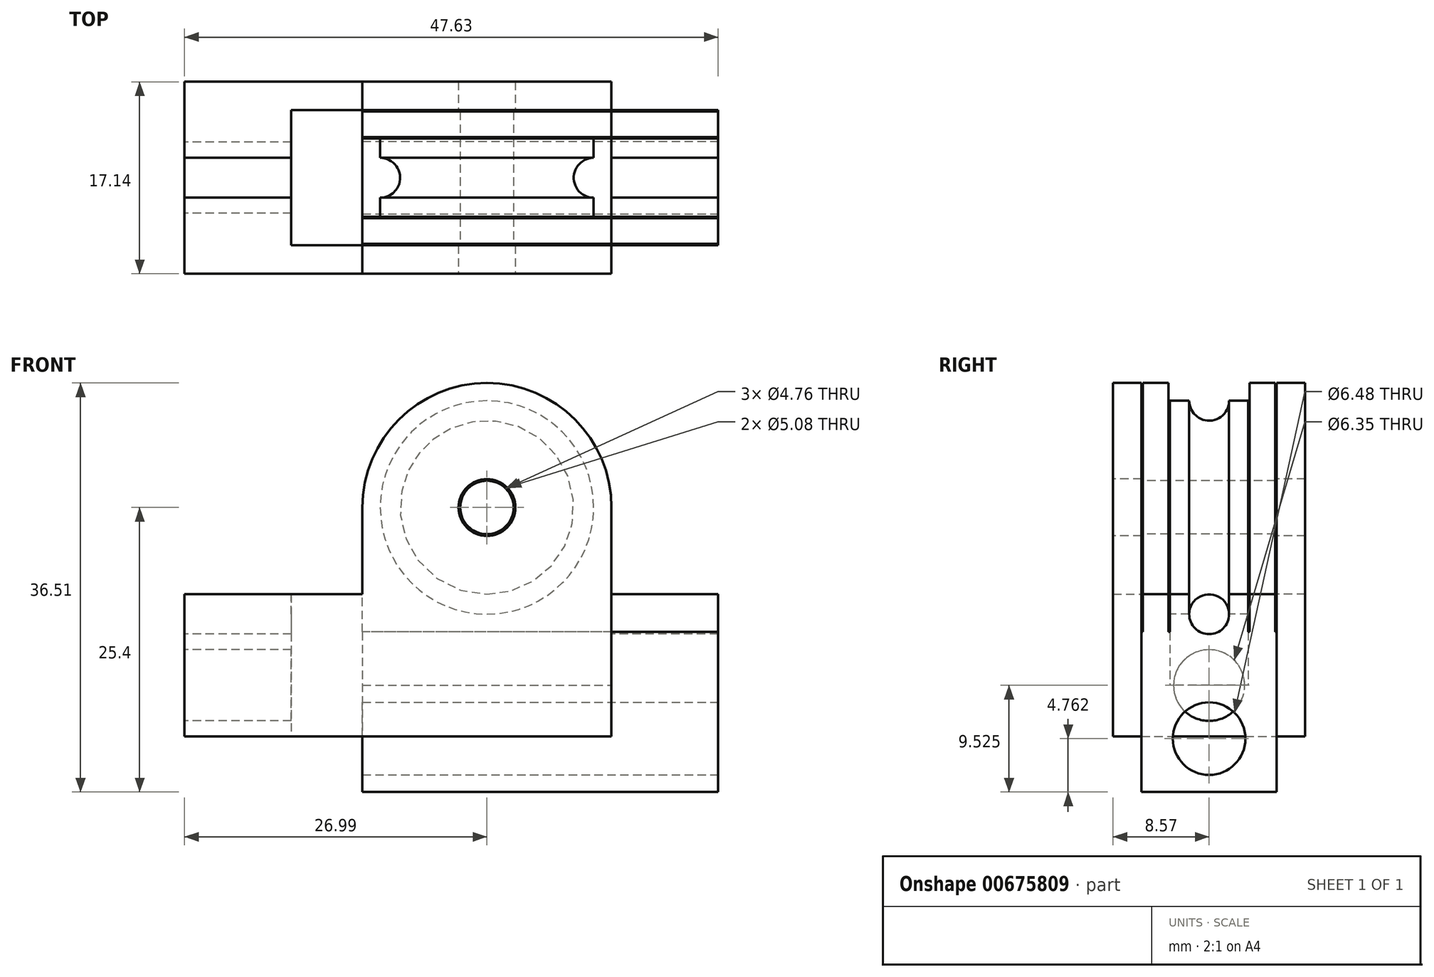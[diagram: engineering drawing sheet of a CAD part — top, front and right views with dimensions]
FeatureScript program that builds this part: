
annotation { "Feature Type Name" : "Feature", "Feature Type Description" : "" }
export const myFeature = defineFeature(function(context is Context, id is Id, definition is map)
    precondition{}
    {
        {
            var Q0;
            Q0=qCreatedBy(makeId("Right.planeOp"),FACE);
            var sketch = newSketch(context, id + "F0", { "sketchPlane" : qUnion([Q0])});
            skLineSegment(sketch, "E0", {"start": v(-3.5, 0) * mm, "end": v(3.5, 0) * mm});
            skLineSegment(sketch, "E1", {"start": v(3.5, 0) * mm, "end": v(3.5, 9.53) * mm});
            skLineSegment(sketch, "E2", {"start": v(3.5, 9.53) * mm, "end": v(1.78, 9.53) * mm});
            skLineSegment(sketch, "E3", {"start": v(-3.5, 0) * mm, "end": v(-3.5, 9.53) * mm});
            skLineSegment(sketch, "E4", {"start": v(-3.5, 9.52) * mm, "end": v(-1.78, 9.52) * mm});
            skArc(sketch, "E5", {"start": v(-1.78, 9.52) * mm, "mid": v(0, 7.75) * mm, "end": v(1.78, 9.52) * mm});
            skSolve(sketch);
        }
        {
            var Q0;
            Q0 = qSketchRegion(id + "F0", true);
            var Q1;
            Q1=sQuery(id+"F0.wireOp",EDGE,"E0");
            revolve(context, id + "F1", {"entities" : qUnion([Q0]), "axis" : qUnion([Q1]), "revolveType" : RevolveType.FULL});
        }
        {
            var Q0;
            Q0=makeQuery(id+"F1.opRevolve","SWEPT_FACE",FACE,{"disambiguationData":[OSD([sQuery(id+"F0.wireOp",EDGE,"E3")])]});
            var sketch = newSketch(context, id + "F2", { "sketchPlane" : qUnion([Q0])});
            skArc(sketch, "E6", {"start": v(11.11, 0) * mm, "mid": v(0, 11.11) * mm, "end": v(-11.11, 0) * mm});
            skLineSegment(sketch, "E7", {"start": v(-11.11, 0) * mm, "end": v(-11.11, -15.88) * mm});
            skLineSegment(sketch, "E8", {"start": v(-11.11, -15.88) * mm, "end": v(11.11, -15.88) * mm});
            skLineSegment(sketch, "E9", {"start": v(11.11, -15.87) * mm, "end": v(11.11, 0) * mm});
            skLineSegment(sketch, "E10", {"start": v(0, -9.52) * mm, "end": v(0, -15.88) * mm, "construction": true});
            skSolve(sketch);
        }
        {
            var Q0;
            Q0 = qSketchRegion(id + "F2", true);
            extrude(context, id + "F3", {"entities" : qUnion([Q0]), "depth" : 2.54 * mm, "offsetDistance" : 25.4 * mm});
        }
        {
            var Q0;
            Q0=makeQuery(id+"F3.opExtrude","SWEPT_BODY",BODY,{"disambiguationData":[OSD([sQuery(id+"F2.wireOp",EDGE,"E6"),sQuery(id+"F2.wireOp",EDGE,"E7"),sQuery(id+"F2.wireOp",EDGE,"E8"),sQuery(id+"F2.wireOp",EDGE,"E9")])]});
            var Q1;
            Q1=qCreatedBy(makeId("Front.planeOp"),FACE);
            mirror(context, id + "F4", {"entities" : qUnion([Q0]), "mirrorPlane" : qUnion([Q1])});
        }
        {
            var Q0;
            Q0=makeQuery(id+"F4.opPattern","COPY",FACE,{"derivedFrom":makeQuery(id+"F3.opExtrude","SWEPT_FACE",FACE,{"disambiguationData":[OSD([sQuery(id+"F2.wireOp",EDGE,"E9")])]}),"instanceName":"1"});
            var sketch = newSketch(context, id + "F5", { "sketchPlane" : qUnion([Q0])});
            skLineSegment(sketch, "E11.bottom", {"start": v(-6.03, -15.88) * mm, "end": v(6.03, -15.88) * mm});
            skLineSegment(sketch, "E11.top", {"start": v(-6.03, -25.4) * mm, "end": v(6.03, -25.4) * mm});
            skLineSegment(sketch, "E11.left", {"start": v(-6.03, -15.88) * mm, "end": v(-6.03, -25.4) * mm});
            skLineSegment(sketch, "E11.right", {"start": v(6.03, -15.88) * mm, "end": v(6.03, -25.4) * mm});
            skSolve(sketch);
        }
        {
            var Q0;
            Q0 = qSketchRegion(id + "F5", true);
            var Q1;
            Q1=makeQuery(id+"F3.opExtrude","SWEPT_FACE",FACE,{"disambiguationData":[OSD([sQuery(id+"F2.wireOp",EDGE,"E7")])]});
            extrude(context, id + "F6", {"entities" : qUnion([Q0]), "operationType" : NewBodyOperationType.ADD, "endBound" : BoundingType.UP_TO_SURFACE, "oppositeDirection" : true, "depth" : 25.4 * mm, "endBoundEntityFace" : qUnion([Q1]), "offsetDistance" : 25.4 * mm});
        }
        {
            var Q0;
            {var subQ0=makeQuery(id+"F3.opExtrude","SWEPT_FACE",FACE,{"disambiguationData":[OSD([sQuery(id+"F2.wireOp",EDGE,"E9")])]});Q0=makeQuery(id+"F6.boolean.opBoolean","MERGE",FACE,{"derivedFrom":[subQ0,makeQuery(id+"F4.opPattern","COPY",FACE,{"derivedFrom":subQ0,"instanceName":"1"}),makeQuery(id+"F6.opExtrude","CAP_FACE",FACE,{"disambiguationData":[OSD([sQuery(id+"F5.wireOp",EDGE,"E11.bottom"),sQuery(id+"F5.wireOp",EDGE,"E11.top"),sQuery(id+"F5.wireOp",EDGE,"E11.left"),sQuery(id+"F5.wireOp",EDGE,"E11.right")])],"isStart":true})]});}
            var sketch = newSketch(context, id + "F7", { "sketchPlane" : qUnion([Q0])});
            skLineSegment(sketch, "E12", {"start": v(-6.03, -25.4) * mm, "end": v(6.03, -15.87) * mm, "construction": true});
            skCircle(sketch, "E13", {"center": v(0, -20.64) * mm, "radius": 3.24 * mm});
            skSolve(sketch);
        }
        {
            var Q0;
            Q0=makeQuery(id+"F7.imprint","IMPRINT",FACE,{"disambiguationData":[TD([[makeQuery(id+"F7.imprint","IMPRINT",EDGE,{"derivedFrom":sQuery(id+"F7.wireOp",EDGE,"E13")}),1.0]])]});
            extrude(context, id + "F8", {"entities" : qUnion([Q0]), "operationType" : NewBodyOperationType.REMOVE, "endBound" : BoundingType.UP_TO_NEXT, "oppositeDirection" : true, "depth" : 25.4 * mm, "offsetDistance" : 25.4 * mm});
        }
        {
            var Q0;
            Q0=makeQuery(id+"F6.boolean.opBoolean","MERGE",FACE,{"derivedFrom":[makeQuery(id+"F3.opExtrude","CAP_FACE",FACE,{"disambiguationData":[OSD([sQuery(id+"F2.wireOp",EDGE,"E6"),sQuery(id+"F2.wireOp",EDGE,"E7"),sQuery(id+"F2.wireOp",EDGE,"E8"),sQuery(id+"F2.wireOp",EDGE,"E9")])],"isStart":false}),makeQuery(id+"F6.opExtrude","SWEPT_FACE",FACE,{"disambiguationData":[OSD([sQuery(id+"F5.wireOp",EDGE,"E11.left")])]})]});
            var sketch = newSketch(context, id + "F9", { "sketchPlane" : qUnion([Q0])});
            skLineSegment(sketch, "E14", {"start": v(-11.11, -20.45) * mm, "end": v(-26.99, -20.45) * mm});
            skCircle(sketch, "E15.0", {"center": v(0, 0) * mm, "radius": 9.53 * mm, "construction": true});
            skCircle(sketch, "E16", {"center": v(0, 0) * mm, "radius": 7.75 * mm, "construction": true});
            skLineSegment(sketch, "E17", {"start": v(-11.11, -7.75) * mm, "end": v(-26.99, -7.75) * mm});
            skArc(sketch, "E18", {"start": v(11.11, 0) * mm, "mid": v(0, 11.11) * mm, "end": v(-11.11, 0) * mm});
            skLineSegment(sketch, "E19", {"start": v(-11.11, 0) * mm, "end": v(-11.11, -7.75) * mm});
            skLineSegment(sketch, "E20", {"start": v(11.11, 0) * mm, "end": v(11.11, -20.45) * mm});
            skLineSegment(sketch, "E21", {"start": v(11.11, -20.45) * mm, "end": v(-11.11, -20.45) * mm});
            skLineSegment(sketch, "E22", {"start": v(-26.99, -7.75) * mm, "end": v(-26.99, -20.45) * mm});
            skSolve(sketch);
        }
        {
            var Q0;
            Q0 = qSketchRegion(id + "F9", true);
            extrude(context, id + "F10", {"entities" : qUnion([Q0]), "depth" : 2.54 * mm, "offsetDistance" : 25.4 * mm});
        }
        {
            var Q0;
            Q0=makeQuery(id+"F10.opExtrude","SWEPT_BODY",BODY,{"disambiguationData":[OSD([sQuery(id+"F9.wireOp",EDGE,"E14"),sQuery(id+"F9.wireOp",EDGE,"E17"),sQuery(id+"F9.wireOp",EDGE,"E18"),sQuery(id+"F9.wireOp",EDGE,"E19"),sQuery(id+"F9.wireOp",EDGE,"E20"),sQuery(id+"F9.wireOp",EDGE,"E21"),sQuery(id+"F9.wireOp",EDGE,"E22")])]});
            var Q1;
            Q1=qCreatedBy(makeId("Front.planeOp"),FACE);
            mirror(context, id + "F11", {"entities" : qUnion([Q0]), "mirrorPlane" : qUnion([Q1])});
        }
        {
            var Q0;
            Q0=makeQuery(id+"F11.opPattern","COPY",FACE,{"derivedFrom":makeQuery(id+"F10.opExtrude","CAP_FACE",FACE,{"disambiguationData":[OSD([sQuery(id+"F9.wireOp",EDGE,"E14"),sQuery(id+"F9.wireOp",EDGE,"E17"),sQuery(id+"F9.wireOp",EDGE,"E18"),sQuery(id+"F9.wireOp",EDGE,"E19"),sQuery(id+"F9.wireOp",EDGE,"E20"),sQuery(id+"F9.wireOp",EDGE,"E21"),sQuery(id+"F9.wireOp",EDGE,"E22")])],"isStart":true}),"instanceName":"1"});
            var sketch = newSketch(context, id + "F12", { "sketchPlane" : qUnion([Q0])});
            skLineSegment(sketch, "E23.bottom", {"start": v(-26.99, -7.75) * mm, "end": v(-17.46, -7.75) * mm});
            skLineSegment(sketch, "E23.top", {"start": v(-26.99, -20.45) * mm, "end": v(-17.46, -20.45) * mm});
            skLineSegment(sketch, "E23.left", {"start": v(-26.99, -7.75) * mm, "end": v(-26.99, -20.45) * mm});
            skLineSegment(sketch, "E23.right", {"start": v(-17.46, -7.75) * mm, "end": v(-17.46, -20.45) * mm});
            skSolve(sketch);
        }
        {
            var Q0;
            Q0 = qSketchRegion(id + "F12", true);
            extrude(context, id + "F13", {"entities" : qUnion([Q0]), "operationType" : NewBodyOperationType.ADD, "endBound" : BoundingType.UP_TO_NEXT, "depth" : 25.4 * mm, "offsetDistance" : 25.4 * mm});
        }
        {
            var Q0;
            {var subQ0=makeQuery(id+"F10.opExtrude","SWEPT_FACE",FACE,{"disambiguationData":[OSD([sQuery(id+"F9.wireOp",EDGE,"E22")])]});Q0=makeQuery(id+"F13.boolean.opBoolean","MERGE",FACE,{"derivedFrom":[subQ0,makeQuery(id+"F11.opPattern","COPY",FACE,{"derivedFrom":subQ0,"instanceName":"1"}),makeQuery(id+"F13.opExtrude","SWEPT_FACE",FACE,{"disambiguationData":[OSD([sQuery(id+"F12.wireOp",EDGE,"E23.left")])]})]});}
            var sketch = newSketch(context, id + "F14", { "sketchPlane" : qUnion([Q0])});
            skLineSegment(sketch, "E24", {"start": v(1.78, 9.52) * mm, "end": v(1.78, -9.52) * mm, "construction": true});
            skLineSegment(sketch, "E25", {"start": v(-1.78, 9.52) * mm, "end": v(-1.78, -9.52) * mm, "construction": true});
            skArc(sketch, "E26", {"start": v(-1.78, 9.52) * mm, "mid": v(0, 7.75) * mm, "end": v(1.78, 9.52) * mm, "construction": true});
            skArc(sketch, "E27", {"start": v(1.78, -9.52) * mm, "mid": v(0, -7.75) * mm, "end": v(-1.78, -9.52) * mm, "construction": true});
            skArc(sketch, "E28", {"start": v(-1.78, -9.52) * mm, "mid": v(0, -11.3) * mm, "end": v(1.78, -9.52) * mm});
            skLineSegment(sketch, "E29", {"start": v(-1.78, -9.52) * mm, "end": v(-1.78, -7.75) * mm});
            skLineSegment(sketch, "E30", {"start": v(-1.78, -7.75) * mm, "end": v(1.78, -7.75) * mm});
            skLineSegment(sketch, "E31", {"start": v(1.78, -7.75) * mm, "end": v(1.78, -9.52) * mm});
            skSolve(sketch);
        }
        {
            var Q0;
            Q0 = qSketchRegion(id + "F14", true);
            extrude(context, id + "F15", {"entities" : qUnion([Q0]), "operationType" : NewBodyOperationType.REMOVE, "endBound" : BoundingType.UP_TO_NEXT, "oppositeDirection" : true, "depth" : 25.4 * mm, "offsetDistance" : 25.4 * mm});
        }
        {
            var Q0;
            {var subQ0=makeQuery(id+"F3.opExtrude","SWEPT_FACE",FACE,{"disambiguationData":[OSD([sQuery(id+"F2.wireOp",EDGE,"E9")])]});Q0=makeQuery(id+"F6.boolean.opBoolean","MERGE",FACE,{"derivedFrom":[subQ0,makeQuery(id+"F4.opPattern","COPY",FACE,{"derivedFrom":subQ0,"instanceName":"1"}),makeQuery(id+"F6.opExtrude","CAP_FACE",FACE,{"disambiguationData":[OSD([sQuery(id+"F5.wireOp",EDGE,"E11.bottom"),sQuery(id+"F5.wireOp",EDGE,"E11.top"),sQuery(id+"F5.wireOp",EDGE,"E11.left"),sQuery(id+"F5.wireOp",EDGE,"E11.right")])],"isStart":true})]});}
            var sketch = newSketch(context, id + "F16", { "sketchPlane" : qUnion([Q0])});
            skLineSegment(sketch, "E32.0.0", {"start": v(1.78, -9.53) * mm, "end": v(1.78, -7.75) * mm});
            skLineSegment(sketch, "E32.0.2", {"start": v(1.78, -7.75) * mm, "end": v(1.78, -9.53) * mm});
            skArc(sketch, "E32.1.1", {"start": v(1.78, -9.53) * mm, "mid": v(0, -11.3) * mm, "end": v(-1.78, -9.53) * mm});
            skArc(sketch, "E32.1.3", {"start": v(1.78, -9.53) * mm, "mid": v(0, -11.3) * mm, "end": v(-1.78, -9.53) * mm});
            skLineSegment(sketch, "E32.2.0", {"start": v(-1.78, -7.75) * mm, "end": v(-1.78, -9.53) * mm});
            skLineSegment(sketch, "E32.2.2", {"start": v(-1.78, -9.53) * mm, "end": v(-1.78, -7.75) * mm});
            skLineSegment(sketch, "E33", {"start": v(-1.78, -7.75) * mm, "end": v(-6.03, -7.75) * mm});
            skLineSegment(sketch, "E34", {"start": v(-6.03, -7.75) * mm, "end": v(-6.03, -25.4) * mm});
            skLineSegment(sketch, "E35", {"start": v(-6.03, -25.4) * mm, "end": v(6.03, -25.4) * mm});
            skLineSegment(sketch, "E36", {"start": v(6.03, -25.4) * mm, "end": v(6.03, -7.75) * mm});
            skLineSegment(sketch, "E37", {"start": v(6.03, -7.75) * mm, "end": v(1.78, -7.75) * mm});
            skCircle(sketch, "E38.0", {"center": v(0, -20.64) * mm, "radius": 3.24 * mm});
            skSolve(sketch);
        }
        {
            var Q0;
            Q0 = qSketchRegion(id + "F16", true);
            extrude(context, id + "F17", {"entities" : qUnion([Q0]), "operationType" : NewBodyOperationType.ADD, "depth" : 9.52 * mm, "offsetDistance" : 25.4 * mm});
        }
        {
            var Q0;
            {var subQ0=makeQuery(id+"F10.opExtrude","SWEPT_FACE",FACE,{"disambiguationData":[OSD([sQuery(id+"F9.wireOp",EDGE,"E22")])]});Q0=makeQuery(id+"F13.boolean.opBoolean","MERGE",FACE,{"derivedFrom":[subQ0,makeQuery(id+"F11.opPattern","COPY",FACE,{"derivedFrom":subQ0,"instanceName":"1"}),makeQuery(id+"F13.opExtrude","SWEPT_FACE",FACE,{"disambiguationData":[OSD([sQuery(id+"F12.wireOp",EDGE,"E23.left")])]})]});}
            var sketch = newSketch(context, id + "F18", { "sketchPlane" : qUnion([Q0])});
            skLineSegment(sketch, "E39", {"start": v(0, -11.3) * mm, "end": v(0, -20.45) * mm, "construction": true});
            skCircle(sketch, "E40", {"center": v(0, -15.88) * mm, "radius": 3.18 * mm});
            skSolve(sketch);
        }
        {
            var Q0;
            Q0=makeQuery(id+"F18.imprint","IMPRINT",FACE,{"disambiguationData":[TD([[makeQuery(id+"F18.imprint","IMPRINT",EDGE,{"derivedFrom":sQuery(id+"F18.wireOp",EDGE,"E40")}),1.0]])]});
            extrude(context, id + "F19", {"entities" : qUnion([Q0]), "operationType" : NewBodyOperationType.REMOVE, "endBound" : BoundingType.UP_TO_NEXT, "oppositeDirection" : true, "depth" : 25.4 * mm, "offsetDistance" : 25.4 * mm});
        }
        {
            var Q0;
            Q0=qCreatedBy(makeId("Right.planeOp"),FACE);
            var sketch = newSketch(context, id + "F20", { "sketchPlane" : qUnion([Q0])});
            skLineSegment(sketch, "E41.bottom", {"start": v(-3.5, 0) * mm, "end": v(-3.62, 0) * mm});
            skLineSegment(sketch, "E41.top", {"start": v(-3.5, 11.11) * mm, "end": v(-3.62, 11.11) * mm});
            skLineSegment(sketch, "E41.left", {"start": v(-3.5, 0) * mm, "end": v(-3.5, 11.11) * mm});
            skLineSegment(sketch, "E41.right", {"start": v(-3.62, 0) * mm, "end": v(-3.62, 11.11) * mm});
            skLineSegment(sketch, "E42.bottom", {"start": v(3.5, 0) * mm, "end": v(3.62, 0) * mm});
            skLineSegment(sketch, "E42.top", {"start": v(3.5, 11.11) * mm, "end": v(3.62, 11.11) * mm});
            skLineSegment(sketch, "E42.left", {"start": v(3.5, 0) * mm, "end": v(3.5, 11.11) * mm});
            skLineSegment(sketch, "E42.right", {"start": v(3.62, 0) * mm, "end": v(3.62, 11.11) * mm});
            skLineSegment(sketch, "E43.bottom", {"start": v(6.03, 0) * mm, "end": v(5.9, 0) * mm});
            skLineSegment(sketch, "E43.top", {"start": v(6.03, 11.11) * mm, "end": v(5.9, 11.11) * mm});
            skLineSegment(sketch, "E43.left", {"start": v(6.03, 0) * mm, "end": v(6.03, 11.11) * mm});
            skLineSegment(sketch, "E43.right", {"start": v(5.9, 0) * mm, "end": v(5.9, 11.11) * mm});
            skLineSegment(sketch, "E44.bottom", {"start": v(-6.03, 0) * mm, "end": v(-5.9, 0) * mm});
            skLineSegment(sketch, "E44.top", {"start": v(-6.03, 11.11) * mm, "end": v(-5.9, 11.11) * mm});
            skLineSegment(sketch, "E44.left", {"start": v(-6.03, 0) * mm, "end": v(-6.03, 11.11) * mm});
            skLineSegment(sketch, "E44.right", {"start": v(-5.9, 0) * mm, "end": v(-5.9, 11.11) * mm});
            skSolve(sketch);
        }
        {
            var Q0;
            Q0 = qSketchRegion(id + "F20", true);
            var Q1;
            Q1=sQuery(id+"F20.wireOp",EDGE,"E41.bottom");
            revolve(context, id + "F21", {"operationType" : NewBodyOperationType.REMOVE, "entities" : qUnion([Q0]), "axis" : qUnion([Q1]), "revolveType" : RevolveType.FULL, "oppositeDirection" : true});
        }
        {
            var Q0;
            {var subQ0=makeQuery(id+"F3.opExtrude","SWEPT_FACE",FACE,{"disambiguationData":[OSD([sQuery(id+"F2.wireOp",EDGE,"E7")])]});Q0=makeQuery(id+"F6.boolean.opBoolean","MERGE",FACE,{"derivedFrom":[subQ0,makeQuery(id+"F4.opPattern","COPY",FACE,{"derivedFrom":subQ0,"instanceName":"1"}),makeQuery(id+"F6.opExtrude","CAP_FACE",FACE,{"disambiguationData":[OSD([sQuery(id+"F5.wireOp",EDGE,"E11.bottom"),sQuery(id+"F5.wireOp",EDGE,"E11.top"),sQuery(id+"F5.wireOp",EDGE,"E11.left"),sQuery(id+"F5.wireOp",EDGE,"E11.right")])],"isStart":false})]});}
            var sketch = newSketch(context, id + "F22", { "sketchPlane" : qUnion([Q0])});
            skLineSegment(sketch, "E45.0", {"start": v(6.03, 0) * mm, "end": v(6.03, -11.11) * mm});
            skLineSegment(sketch, "E45.1", {"start": v(-6.03, 0) * mm, "end": v(-6.03, -11.11) * mm});
            skLineSegment(sketch, "E46.bottom", {"start": v(-6.03, -11.11) * mm, "end": v(-5.9, -11.11) * mm});
            skLineSegment(sketch, "E46.top", {"start": v(-6.03, 0) * mm, "end": v(-5.9, 0) * mm});
            skLineSegment(sketch, "E46.left", {"start": v(-6.03, -11.11) * mm, "end": v(-6.03, 0) * mm});
            skLineSegment(sketch, "E46.right", {"start": v(-5.9, -11.11) * mm, "end": v(-5.9, 0) * mm});
            skLineSegment(sketch, "E47.bottom", {"start": v(6.03, -11.11) * mm, "end": v(5.9, -11.11) * mm});
            skLineSegment(sketch, "E47.top", {"start": v(6.03, 0) * mm, "end": v(5.9, 0) * mm});
            skLineSegment(sketch, "E47.left", {"start": v(6.03, -11.11) * mm, "end": v(6.03, 0) * mm});
            skLineSegment(sketch, "E47.right", {"start": v(5.9, -11.11) * mm, "end": v(5.9, 0) * mm});
            skLineSegment(sketch, "E48.bottom", {"start": v(-3.5, -11.11) * mm, "end": v(-3.62, -11.11) * mm});
            skLineSegment(sketch, "E48.top", {"start": v(-3.5, 0) * mm, "end": v(-3.62, 0) * mm});
            skLineSegment(sketch, "E48.left", {"start": v(-3.5, -11.11) * mm, "end": v(-3.5, 0) * mm});
            skLineSegment(sketch, "E48.right", {"start": v(-3.62, -11.11) * mm, "end": v(-3.62, 0) * mm});
            skLineSegment(sketch, "E49.bottom", {"start": v(3.5, -11.11) * mm, "end": v(3.62, -11.11) * mm});
            skLineSegment(sketch, "E49.top", {"start": v(3.5, 0) * mm, "end": v(3.62, 0) * mm});
            skLineSegment(sketch, "E49.left", {"start": v(3.5, -11.11) * mm, "end": v(3.5, 0) * mm});
            skLineSegment(sketch, "E49.right", {"start": v(3.62, -11.11) * mm, "end": v(3.62, 0) * mm});
            skSolve(sketch);
        }
        {
            var Q0;
            Q0 = qSketchRegion(id + "F22", true);
            extrude(context, id + "F23", {"entities" : qUnion([Q0]), "operationType" : NewBodyOperationType.REMOVE, "endBound" : BoundingType.THROUGH_ALL, "oppositeDirection" : true, "depth" : 25.4 * mm, "offsetDistance" : 25.4 * mm});
        }
        {
            var Q0;
            Q0=qCreatedBy(makeId("Right.planeOp"),FACE);
            var sketch = newSketch(context, id + "F24", { "sketchPlane" : qUnion([Q0])});
            skLineSegment(sketch, "E50", {"start": v(8.57, 0) * mm, "end": v(-8.57, 0) * mm});
            skLineSegment(sketch, "E51", {"start": v(-8.57, 0) * mm, "end": v(-8.57, 2.54) * mm});
            skLineSegment(sketch, "E52", {"start": v(-8.57, 2.54) * mm, "end": v(-6.03, 2.54) * mm});
            skLineSegment(sketch, "E53", {"start": v(-6.03, 2.54) * mm, "end": v(-6.03, 2.38) * mm});
            skLineSegment(sketch, "E54", {"start": v(-6.03, 2.38) * mm, "end": v(6.03, 2.38) * mm});
            skLineSegment(sketch, "E55", {"start": v(6.03, 2.38) * mm, "end": v(6.03, 2.54) * mm});
            skLineSegment(sketch, "E56", {"start": v(6.03, 2.54) * mm, "end": v(8.57, 2.54) * mm});
            skLineSegment(sketch, "E57", {"start": v(8.57, 2.54) * mm, "end": v(8.57, 0) * mm});
            skSolve(sketch);
        }
        {
            var Q0;
            Q0 = qSketchRegion(id + "F24", true);
            var Q1;
            Q1=sQuery(id+"F24.wireOp",EDGE,"E50");
            revolve(context, id + "F25", {"operationType" : NewBodyOperationType.REMOVE, "entities" : qUnion([Q0]), "axis" : qUnion([Q1]), "revolveType" : RevolveType.FULL, "oppositeDirection" : true});
        }
    });
